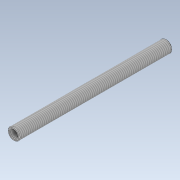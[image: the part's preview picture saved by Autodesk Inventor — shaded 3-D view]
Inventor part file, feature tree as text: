
AUTODESK INVENTOR PART (.ipt)
format: ipt  version: 2021 (Build 250183000, 183)  size: 95,232 bytes
history: native  units: mm
features: other x1, revolve x1, thread x1, chamfer x1, sketch x1
ambient origin geometry x8: Origin, YZ Plane, XZ Plane, XY Plane, X Axis, Y Axis, Z Axis, Center Point
bodies: Body1 (feature_tree)
feature tree (5):
  other  "Sólido1"
  revolve  "Revolución1"  [1 undecoded]
  thread  "Rosca1"  [1 undecoded]
  chamfer  "Chaflán1"  Angle=90.0deg  [1 undecoded]
  sketch  "Boceto1"  dims[d0=129.0mm d1=10.0mm d3=2.0mm d4=90.0deg d5=100.0mm d6=0.0mm d7=0.5mm d8=2.0mm d9=45.0deg]
note: 3 required parameter values undecoded (feature->parameter linkage not recoverable at this tier; creation-order binding heuristic only, values carry confidence <= 0.55)